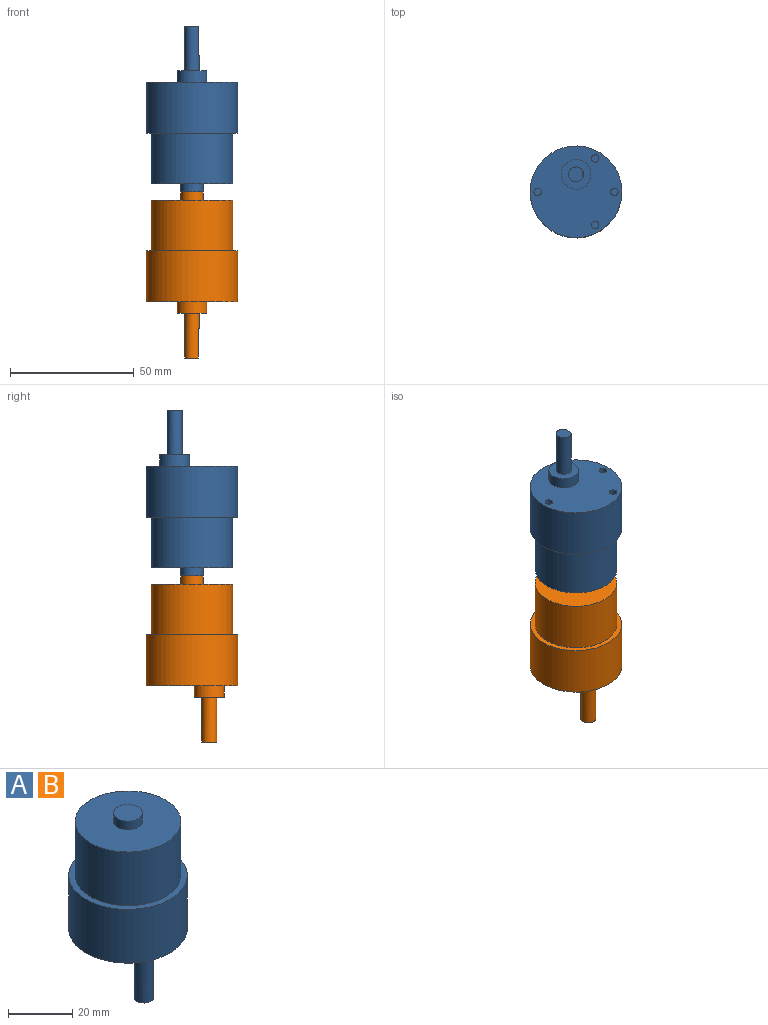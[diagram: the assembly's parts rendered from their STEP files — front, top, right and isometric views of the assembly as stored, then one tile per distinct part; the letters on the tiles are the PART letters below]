
ASSEMBLY  parts=2 mates=1
PART A: 21 faces, bbox 37x37x67 mm
  f0: plane 6x5.5mm, normal (0,0,-1), area 27.1mm2, adj f8,f9
  f1: cylinder r=16.5mm len=33mm, axis (0,0,-1), area 2125.3mm2, adj f2,f5
  f2: plane 33x33mm, normal (0,0,1), area 791.7mm2, adj f1,f19
  f3: cylinder r=18.5mm len=37mm, axis (0,0,1), area 2382.9mm2, adj f4,f5
  f4: plane 37x37mm, normal (0,0,-1), area 933.8mm2, adj f3,f6,f11,f13,f15,f17
  f5: plane 37x37mm, normal (0,0,1), area 219.9mm2, adj f1,f3
  f6: cylinder r=6mm len=12mm, axis (0,0,1), area 173.4mm2, adj f4,f7
  f7: plane 12x12mm, normal (0,0,-1), area 84.8mm2, adj f6,f8
  f8: cylinder r=3mm len=18.1mm, axis (0,0,1), area 299mm2, adj f0,f7,f9,f10
  f9: plane 12x3.32mm, normal (1,0,0), area 39.8mm2, adj f0,f8,f10
  f10: plane 3.32x0.5mm, normal (0,0,-1), area 1.1mm2, adj f8,f9
  f11: cylinder r=1.5mm len=4mm, axis (0,0,-1), area 37.7mm2, adj f4,f12
  f12: plane 3x3mm, normal (0,0,-1), area 7.1mm2, adj f11
  f13: cylinder r=1.5mm len=4mm, axis (0,0,-1), area 37.7mm2, adj f4,f14
  f14: plane 3x3mm, normal (0,0,-1), area 7.1mm2, adj f13
  f15: cylinder r=1.5mm len=4mm, axis (0,0,-1), area 37.7mm2, adj f4,f16
  f16: plane 3x3mm, normal (0,0,-1), area 7.1mm2, adj f15
  f17: cylinder r=1.5mm len=4mm, axis (0,0,-1), area 37.7mm2, adj f4,f18
  f18: plane 3x3mm, normal (0,0,-1), area 7.1mm2, adj f17
  f19: cylinder r=4.5mm len=9mm, axis (0,0,-1), area 93.3mm2, adj f2,f20
  f20: plane 9x9mm, normal (0,0,1), area 63.6mm2, adj f19
PART B: same geometry as A
PLACE A rot(axis=(1,0,0),180deg) t=(-4.28,-27.94,68.9)mm
PLACE B t=(-4.28,-27.94,21.3)mm
MATE fastened A.f19 <-> B.f19  axis (0,0,-1) through (-4.28,-27.94,45.1)mm
